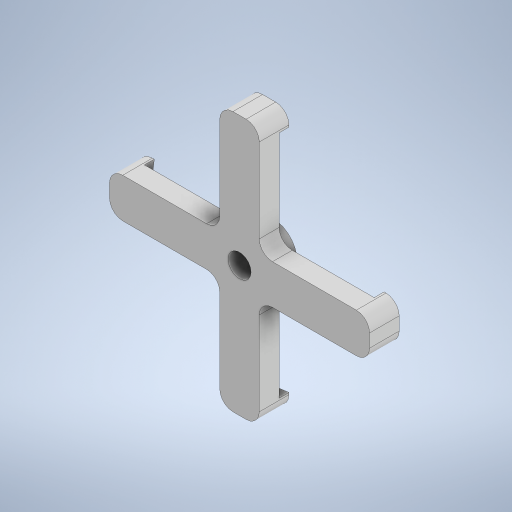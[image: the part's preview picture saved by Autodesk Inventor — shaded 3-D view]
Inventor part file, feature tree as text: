
AUTODESK INVENTOR PART (.ipt)
format: ipt  version: 2023 (Build 270158000, 158)  size: 340,992 bytes
history: native  units: in
note: dims shown in document units (in); Inventor stores cm internally (conversion verified against a paired STEP export)
features: extrude x5, sketch x5, other x4, reference x4, fillet x2, projected_geometry x2
ambient origin geometry x8: Origin, YZ Plane, XZ Plane, XY Plane, X Axis, Y Axis, Z Axis, Center Point
bodies: Body1 (feature_tree)
feature tree (22):
  other  "Bryła1"
  extrude  "Wyciągnięcie proste1"  Depth=0.2362in
  extrude  "Wyciągnięcie proste2"  Depth=0.2362in
  sketch  "Szkic3"
  other  "Płaszczyzna konstrukcyjna1"
  extrude  "Wyciągnięcie proste3"  Depth=0.1378in
  extrude  "Wyciągnięcie proste4"  Depth=0.1181in TaperAngle=0.0deg
  extrude  "Wyciągnięcie proste5"  Depth=0.1378in
  fillet  "Zaokrąglenie1"  [1 undecoded]
  fillet  "Zaokrąglenie2"  Radius=0.0787in
  sketch  "Szkic1"
  reference  "Odniesienie1"
  reference  "Odniesienie2"
  sketch  "Szkic2"
  sketch  "Szkic4"
  reference  "Odniesienie3"
  projected_geometry  "Pętla rzutowana1"
  sketch  "Szkic5"
  reference  "Odniesienie4"
  projected_geometry  "Pętla rzutowana2"
  other  "Zespół2"
  other  "podstawa_formy:1"
note: 1 required parameter value undecoded (feature->parameter linkage not recoverable at this tier; creation-order binding heuristic only, values carry confidence <= 0.55)
